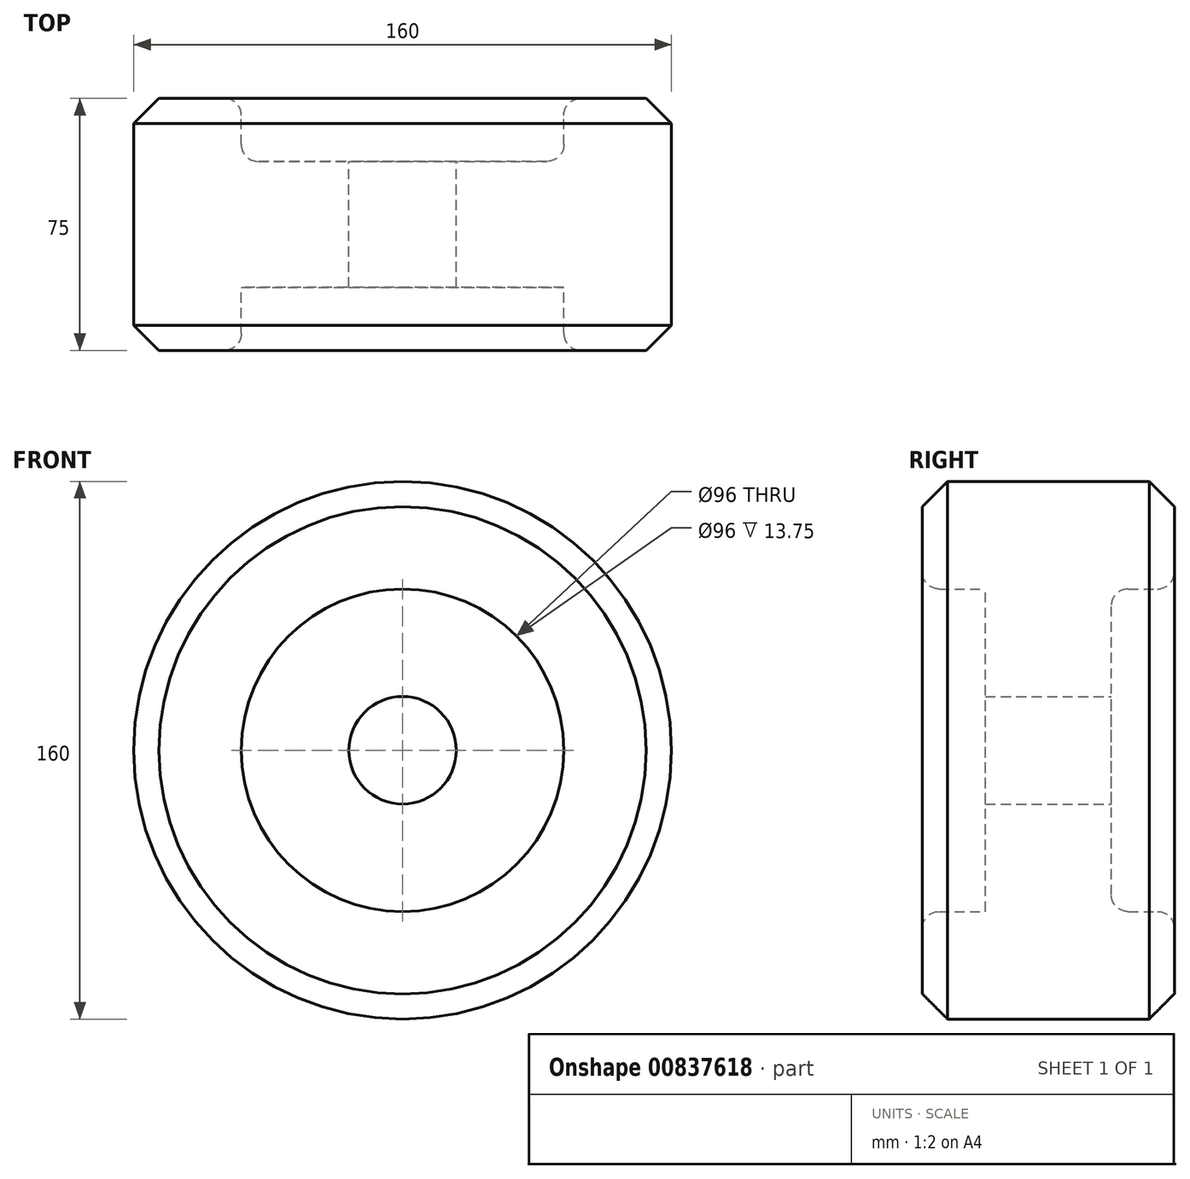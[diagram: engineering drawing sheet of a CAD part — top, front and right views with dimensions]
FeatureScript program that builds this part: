
annotation { "Feature Type Name" : "Feature", "Feature Type Description" : "" }
export const myFeature = defineFeature(function(context is Context, id is Id, definition is map)
    precondition{}
    {
        {
            var Q0;
            Q0=qCreatedBy(makeId("Front.planeOp"),FACE);
            var sketch = newSketch(context, id + "F0", { "sketchPlane" : qUnion([Q0])});
            skCircle(sketch, "E0", {"center": v(0, 0) * mm, "radius": 16 * mm});
            skCircle(sketch, "E1", {"center": v(0, 0) * mm, "radius": 48 * mm});
            skCircle(sketch, "E2", {"center": v(0, 0) * mm, "radius": 80 * mm});
            skSolve(sketch);
        }
        {
            var Q0;
            Q0=makeQuery(id+"F0.imprint","IMPRINT",FACE,{"disambiguationData":[TD([[makeQuery(id+"F0.imprint","IMPRINT",EDGE,{"derivedFrom":sQuery(id+"F0.wireOp",EDGE,"E0")}),-1.0]])]});
            extrude(context, id + "F1", {"entities" : qUnion([Q0]), "endBound" : BoundingType.SYMMETRIC, "depth" : 37.5 * mm, "offsetDistance" : 25 * mm});
        }
        {
            var Q0;
            Q0=makeQuery(id+"F0.imprint","IMPRINT",FACE,{"disambiguationData":[TD([[makeQuery(id+"F0.imprint","IMPRINT",EDGE,{"derivedFrom":sQuery(id+"F0.wireOp",EDGE,"E1")}),-1.0]])]});
            extrude(context, id + "F2", {"entities" : qUnion([Q0]), "operationType" : NewBodyOperationType.ADD, "endBound" : BoundingType.SYMMETRIC, "depth" : 75 * mm, "offsetDistance" : 25 * mm});
        }
        {
            var Q0;
            Q0=makeQuery(id+"F2.opExtrude","CAP_EDGE",EDGE,{"disambiguationData":[OSD([sQuery(id+"F0.wireOp",EDGE,"E2")])],"isStart":true});
            var Q1;
            Q1=makeQuery(id+"F2.opExtrude","CAP_EDGE",EDGE,{"disambiguationData":[OSD([sQuery(id+"F0.wireOp",EDGE,"E2")])],"isStart":false});
            chamfer(context, id + "F3", {"entities" : qUnion([Q0, Q1]), "width" : 7.5 * mm, "tangentPropagation" : true});
        }
        {
            var Q0;
            Q0=makeQuery(id+"F2.opExtrude","CAP_EDGE",EDGE,{"disambiguationData":[OSD([sQuery(id+"F0.wireOp",EDGE,"E1")])],"isStart":false});
            var Q1;
            Q1=makeQuery(id+"F2.opExtrude","CAP_EDGE",EDGE,{"disambiguationData":[OSD([sQuery(id+"F0.wireOp",EDGE,"E1")])],"isStart":true});
            var Q2;
            Q2=makeQuery(id+"F1.opExtrude","CAP_EDGE",EDGE,{"disambiguationData":[OSD([sQuery(id+"F0.wireOp",EDGE,"E1")])],"isStart":true});
            var Q3;
            Q3=makeQuery(id+"F1.opExtrude","CAP_EDGE",EDGE,{"disambiguationData":[OSD([sQuery(id+"F0.wireOp",EDGE,"E1")])],"isStart":false});
            fillet(context, id + "F4", {"entities" : qUnion([Q0, Q1, Q2, Q3]), "radius" : 5 * mm, "tangentPropagation" : true, "allowEdgeOverflow" : false});
        }
    });
